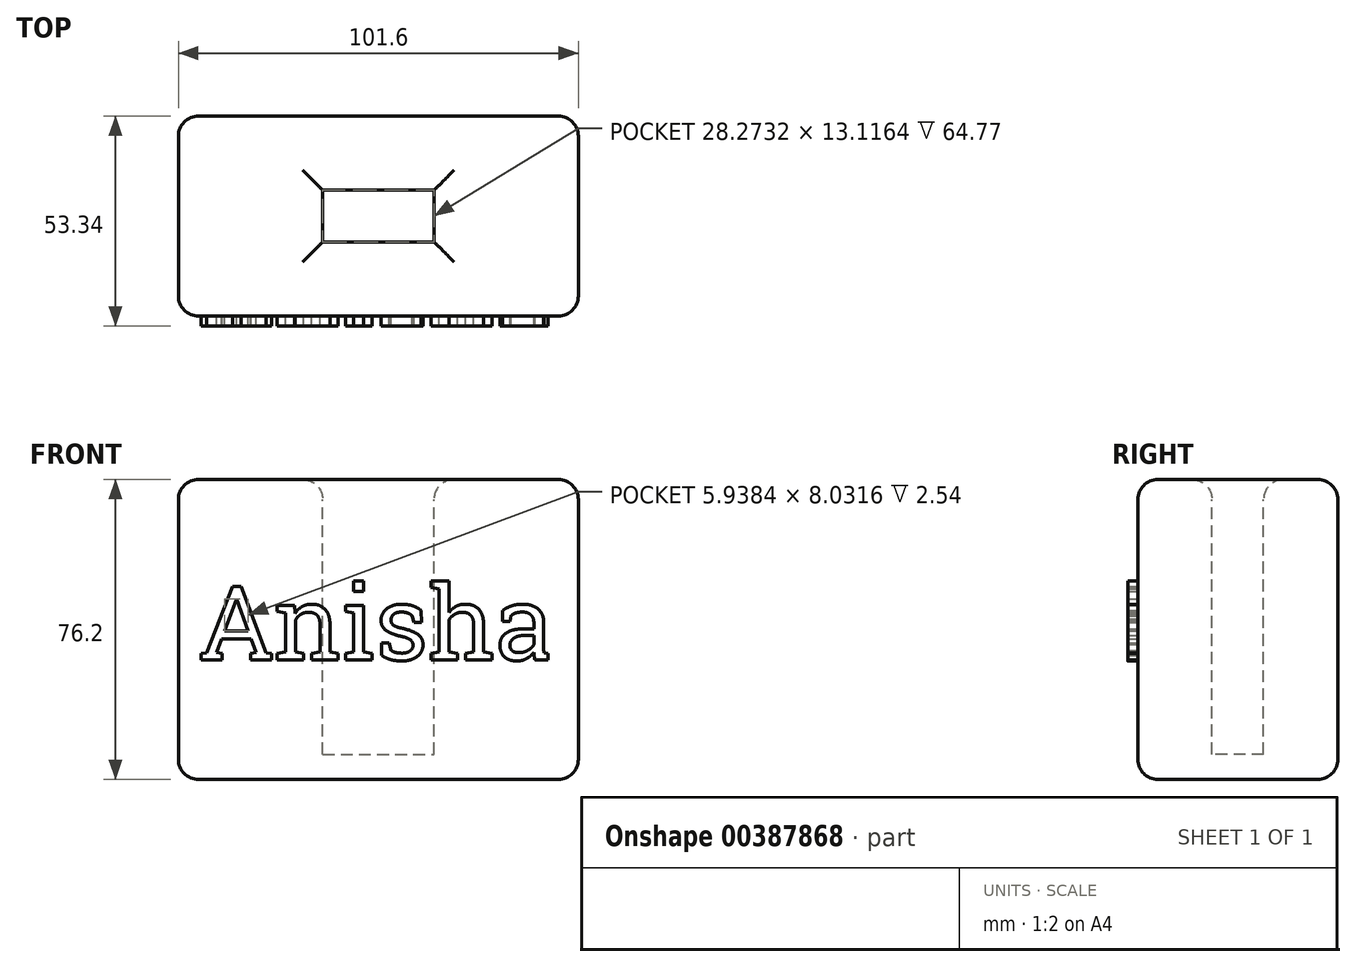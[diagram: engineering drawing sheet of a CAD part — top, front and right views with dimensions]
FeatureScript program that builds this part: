
annotation { "Feature Type Name" : "Feature", "Feature Type Description" : "" }
export const myFeature = defineFeature(function(context is Context, id is Id, definition is map)
    precondition{}
    {
        {
            var Q0;
            Q0=qCreatedBy(makeId("Top.planeOp"),FACE);
            var sketch = newSketch(context, id + "F0", { "sketchPlane" : qUnion([Q0])});
            skLineSegment(sketch, "E0.bottom", {"start": v(-50.8, -25.4) * mm, "end": v(50.8, -25.4) * mm});
            skLineSegment(sketch, "E0.top", {"start": v(-50.8, 25.4) * mm, "end": v(50.8, 25.4) * mm});
            skLineSegment(sketch, "E0.left", {"start": v(-50.8, -25.4) * mm, "end": v(-50.8, 25.4) * mm});
            skLineSegment(sketch, "E0.right", {"start": v(50.8, -25.4) * mm, "end": v(50.8, 25.4) * mm});
            skPoint(sketch, "E0.middle", {"position": v(0, 0) * mm});
            skSolve(sketch);
        }
        {
            var Q0;
            Q0 = qSketchRegion(id + "F0", true);
            extrude(context, id + "F1", {"entities" : qUnion([Q0]), "depth" : 76.2 * mm});
        }
        {
            var Q0;
            Q0=makeQuery(id+"F1.opExtrude","CAP_FACE",FACE,{"disambiguationData":[OSD([sQuery(id+"F0.wireOp",EDGE,"E0.bottom"),sQuery(id+"F0.wireOp",EDGE,"E0.top"),sQuery(id+"F0.wireOp",EDGE,"E0.left"),sQuery(id+"F0.wireOp",EDGE,"E0.right")])],"isStart":true});
            fillet(context, id + "F2", {"entities" : qUnion([Q0]), "radius" : 5.08 * mm, "tangentPropagation" : true, "allowEdgeOverflow" : false});
        }
        {
            var Q0;
            Q0=makeQuery(id+"F1.opExtrude","SWEPT_FACE",FACE,{"disambiguationData":[OSD([sQuery(id+"F0.wireOp",EDGE,"E0.bottom")])]});
            fillet(context, id + "F3", {"entities" : qUnion([Q0]), "radius" : 5.08 * mm, "tangentPropagation" : true, "allowEdgeOverflow" : false});
        }
        {
            var Q0;
            Q0=makeQuery(id+"F1.opExtrude","SWEPT_FACE",FACE,{"disambiguationData":[OSD([sQuery(id+"F0.wireOp",EDGE,"E0.left")])]});
            var Q1;
            Q1=makeQuery(id+"F1.opExtrude","SWEPT_FACE",FACE,{"disambiguationData":[OSD([sQuery(id+"F0.wireOp",EDGE,"E0.top")])]});
            var Q2;
            Q2=makeQuery(id+"F1.opExtrude","SWEPT_FACE",FACE,{"disambiguationData":[OSD([sQuery(id+"F0.wireOp",EDGE,"E0.right")])]});
            fillet(context, id + "F4", {"entities" : qUnion([Q0, Q1, Q2]), "radius" : 5.08 * mm, "tangentPropagation" : true, "allowEdgeOverflow" : false});
        }
        {
            var Q0;
            Q0=makeQuery(id+"F1.opExtrude","SWEPT_FACE",FACE,{"disambiguationData":[OSD([sQuery(id+"F0.wireOp",EDGE,"E0.bottom")])]});
            var sketch = newSketch(context, id + "F5", { "sketchPlane" : qUnion([Q0])});
            skText(sketch, "E1", { "text": "Anisha", "fontName": "RobotoSlab-Regular.ttf"});
            const initialGuessF5  = {"E1": [-0.04572, 0.03036, 1, 0, 0.01895]};
            skSetInitialGuess(sketch, initialGuessF5);
            skSolve(sketch);
        }
        {
            var Q0;
            Q0 = qSketchRegion(id + "F5", true);
            extrude(context, id + "F6", {"entities" : qUnion([Q0]), "operationType" : NewBodyOperationType.ADD, "depth" : 2.54 * mm});
        }
        {
            var Q0;
            Q0=makeQuery(id+"F1.opExtrude","CAP_FACE",FACE,{"disambiguationData":[OSD([sQuery(id+"F0.wireOp",EDGE,"E0.bottom"),sQuery(id+"F0.wireOp",EDGE,"E0.top"),sQuery(id+"F0.wireOp",EDGE,"E0.left"),sQuery(id+"F0.wireOp",EDGE,"E0.right")])],"isStart":false});
            var sketch = newSketch(context, id + "F7", { "sketchPlane" : qUnion([Q0])});
            skLineSegment(sketch, "E2.bottom", {"start": v(-10.2, 3.64) * mm, "end": v(10.2, 3.64) * mm});
            skLineSegment(sketch, "E2.top", {"start": v(-10.2, -3.64) * mm, "end": v(10.2, -3.64) * mm});
            skLineSegment(sketch, "E2.left", {"start": v(-10.2, 3.64) * mm, "end": v(-10.2, -3.64) * mm});
            skLineSegment(sketch, "E2.right", {"start": v(10.2, 3.64) * mm, "end": v(10.2, -3.64) * mm});
            skPoint(sketch, "E2.middle", {"position": v(0, 0) * mm});
            skSolve(sketch);
        }
        {
            var Q0;
            Q0=makeQuery(id+"F7.imprint","IMPRINT",FACE,{"disambiguationData":[TD([[makeQuery(id+"F7.imprint","IMPRINT",EDGE,{"derivedFrom":sQuery(id+"F7.wireOp",EDGE,"E2.bottom")}),-1.0]])]});
            extrude(context, id + "F8", {"entities" : qUnion([Q0]), "operationType" : NewBodyOperationType.ADD, "depth" : 25.4 * mm});
        }
        {
            var Q0;
            Q0=makeQuery(id+"F8.opExtrude","CAP_FACE",FACE,{"disambiguationData":[OSD([sQuery(id+"F7.wireOp",EDGE,"E2.bottom"),sQuery(id+"F7.wireOp",EDGE,"E2.top"),sQuery(id+"F7.wireOp",EDGE,"E2.left"),sQuery(id+"F7.wireOp",EDGE,"E2.right")])],"isStart":false});
            extrude(context, id + "F9", {"entities" : qUnion([Q0]), "operationType" : NewBodyOperationType.REMOVE, "oppositeDirection" : true, "depth" : 25.4 * mm});
        }
        {
            var Q0;
            Q0=makeQuery(id+"F9.boolean.opBoolean","MERGE",FACE,{"derivedFrom":[makeQuery(id+"F1.opExtrude","CAP_FACE",FACE,{"disambiguationData":[OSD([sQuery(id+"F0.wireOp",EDGE,"E0.bottom"),sQuery(id+"F0.wireOp",EDGE,"E0.top"),sQuery(id+"F0.wireOp",EDGE,"E0.left"),sQuery(id+"F0.wireOp",EDGE,"E0.right")])],"isStart":false}),makeQuery(id+"F9.opExtrude","CAP_FACE",FACE,{"disambiguationData":[OSD([sQuery(id+"F7.wireOp",EDGE,"E2.bottom"),sQuery(id+"F7.wireOp",EDGE,"E2.top"),sQuery(id+"F7.wireOp",EDGE,"E2.left"),sQuery(id+"F7.wireOp",EDGE,"E2.right")])],"isStart":false})]});
            var sketch = newSketch(context, id + "F10", { "sketchPlane" : qUnion([Q0])});
            skLineSegment(sketch, "E3.bottom", {"start": v(-14.14, 6.56) * mm, "end": v(14.14, 6.56) * mm});
            skLineSegment(sketch, "E3.top", {"start": v(-14.14, -6.56) * mm, "end": v(14.14, -6.56) * mm});
            skLineSegment(sketch, "E3.left", {"start": v(-14.14, 6.56) * mm, "end": v(-14.14, -6.56) * mm});
            skLineSegment(sketch, "E3.right", {"start": v(14.14, 6.56) * mm, "end": v(14.14, -6.56) * mm});
            skPoint(sketch, "E3.middle", {"position": v(0, 0) * mm});
            skSolve(sketch);
        }
        {
            var Q0;
            Q0 = qSketchRegion(id + "F10", true);
            extrude(context, id + "F11", {"entities" : qUnion([Q0]), "operationType" : NewBodyOperationType.REMOVE, "oppositeDirection" : true, "depth" : 69.85 * mm});
        }
        {
            var Q0;
            Q0=makeQuery(id+"F9.boolean.opBoolean","MERGE",FACE,{"derivedFrom":[makeQuery(id+"F1.opExtrude","CAP_FACE",FACE,{"disambiguationData":[OSD([sQuery(id+"F0.wireOp",EDGE,"E0.bottom"),sQuery(id+"F0.wireOp",EDGE,"E0.top"),sQuery(id+"F0.wireOp",EDGE,"E0.left"),sQuery(id+"F0.wireOp",EDGE,"E0.right")])],"isStart":false}),makeQuery(id+"F9.opExtrude","CAP_FACE",FACE,{"disambiguationData":[OSD([sQuery(id+"F7.wireOp",EDGE,"E2.bottom"),sQuery(id+"F7.wireOp",EDGE,"E2.top"),sQuery(id+"F7.wireOp",EDGE,"E2.left"),sQuery(id+"F7.wireOp",EDGE,"E2.right")])],"isStart":false})]});
            fillet(context, id + "F12", {"entities" : qUnion([Q0]), "radius" : 5.08 * mm, "tangentPropagation" : true, "allowEdgeOverflow" : false});
        }
    });
